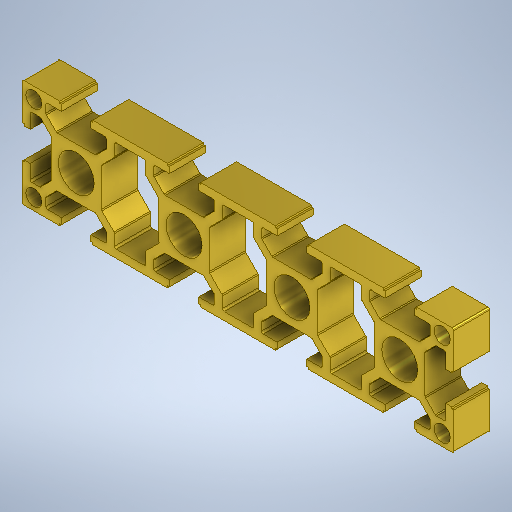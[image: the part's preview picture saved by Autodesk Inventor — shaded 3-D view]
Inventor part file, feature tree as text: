
AUTODESK INVENTOR PART (.ipt)
format: ipt  version: 2025.2 (Build 292293000, 293)  size: 653,312 bytes
history: native  units: mm
features: mirror x2, other x1, extrude x1, sketch x1
ambient origin geometry x8: Origin, YZ Plane, XZ Plane, XY Plane, X Axis, Y Axis, Z Axis, Center Point
bodies: Body1 (feature_tree)
feature tree (5):
  other  "Sólido1"
  extrude  "Extrusão1"  Depth=15.0mm
  mirror  "Espelhar1"
  mirror  "Espelhar2"
  sketch  "Esboço2"  dims[d45=10.0mm d46=15.0mm d48=15.0mm d49=15.0mm d50=8.2mm d51=8.0mm d55=2.2mm d61=1.1mm d62=1.1mm d64=30.0mm d75=2.2mm d81=4.5mm d83=1.1mm d86=10.0mm d87=0.0mm]
